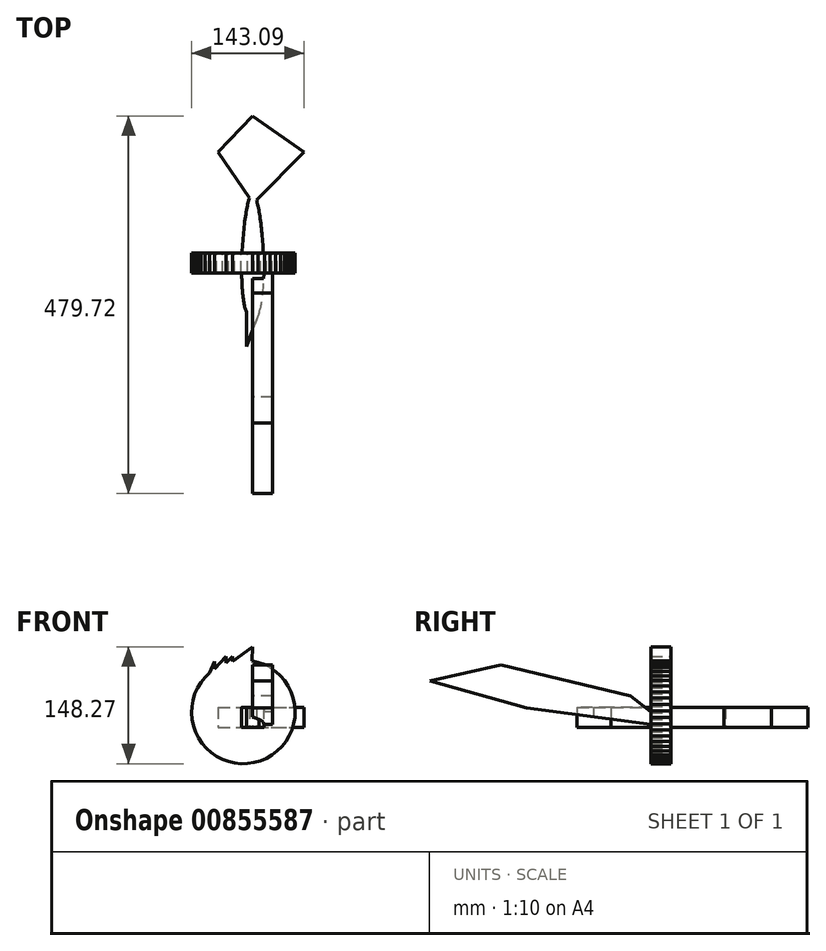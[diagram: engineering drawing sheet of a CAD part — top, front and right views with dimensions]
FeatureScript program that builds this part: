
annotation { "Feature Type Name" : "Feature", "Feature Type Description" : "" }
export const myFeature = defineFeature(function(context is Context, id is Id, definition is map)
    precondition{}
    {
        {
            var Q0;
            Q0=qCreatedBy(makeId("Top.planeOp"),FACE);
            var sketch = newSketch(context, id + "F0", { "sketchPlane" : qUnion([Q0])});
            skFitSpline(sketch, "E0", {"points": [v(0, 75.5) * mm, v(-7.53, -76.07) * mm, v(7.83, -76.02) * mm, v(0, 75.5) * mm]});
            skLineSegment(sketch, "E1", {"start": v(-7.53, -76.07) * mm, "end": v(-7.53, -118.78) * mm});
            skLineSegment(sketch, "E2", {"start": v(-7.53, -118.78) * mm, "end": v(7.83, -76.02) * mm});
            skLineSegment(sketch, "E3", {"start": v(-4.05, 69.83) * mm, "end": v(10.3, 128.02) * mm});
            skLineSegment(sketch, "E4", {"start": v(10.3, 128.02) * mm, "end": v(4.84, 67.53) * mm});
            skLineSegment(sketch, "E5", {"start": v(4.84, 67.53) * mm, "end": v(65.48, 128.02) * mm});
            skLineSegment(sketch, "E6", {"start": v(65.48, 128.02) * mm, "end": v(-44.03, 128.02) * mm});
            skLineSegment(sketch, "E7", {"start": v(-44.03, 128.02) * mm, "end": v(-4.05, 69.83) * mm});
            skLineSegment(sketch, "E8", {"start": v(-44.03, 128.02) * mm, "end": v(0, 174.22) * mm});
            skLineSegment(sketch, "E9", {"start": v(0, 174.22) * mm, "end": v(65.48, 128.02) * mm});
            skSolve(sketch);
        }
        {
            var Q0;
            Q0 = qSketchRegion(id + "F0", true);
            extrude(context, id + "F1", {"entities" : qUnion([Q0]), "depth" : 25.4 * mm, "offsetDistance" : 25.4 * mm});
        }
        {
            var Q0;
            Q0=qCreatedBy(makeId("Front.planeOp"),FACE);
            var sketch = newSketch(context, id + "F2", { "sketchPlane" : qUnion([Q0])});
            skCircle(sketch, "E10.cCircle", {"center": v(-11.87, 19.5) * mm, "radius": 65.76 * mm, "construction": true});
            skLineSegment(sketch, "E10.0", {"start": v(28.92, 71.09) * mm, "end": v(35.06, 65.57) * mm});
            skLineSegment(sketch, "E10.1", {"start": v(35.06, 65.57) * mm, "end": v(40.47, 59.32) * mm});
            skLineSegment(sketch, "E10.2", {"start": v(40.47, 59.32) * mm, "end": v(45.04, 52.45) * mm});
            skLineSegment(sketch, "E10.3", {"start": v(45.04, 52.45) * mm, "end": v(48.72, 45.05) * mm});
            skLineSegment(sketch, "E10.4", {"start": v(48.72, 45.05) * mm, "end": v(51.45, 37.26) * mm});
            skLineSegment(sketch, "E10.5", {"start": v(51.45, 37.26) * mm, "end": v(53.17, 29.18) * mm});
            skLineSegment(sketch, "E10.6", {"start": v(53.17, 29.18) * mm, "end": v(53.87, 20.95) * mm});
            skLineSegment(sketch, "E10.7", {"start": v(53.87, 20.95) * mm, "end": v(53.54, 12.7) * mm});
            skLineSegment(sketch, "E10.8", {"start": v(53.54, 12.7) * mm, "end": v(52.17, 4.56) * mm});
            skLineSegment(sketch, "E10.9", {"start": v(52.17, 4.56) * mm, "end": v(49.8, -3.35) * mm});
            skLineSegment(sketch, "E10.10", {"start": v(49.8, -3.35) * mm, "end": v(46.44, -10.9) * mm});
            skLineSegment(sketch, "E10.11", {"start": v(46.44, -10.9) * mm, "end": v(42.17, -17.96) * mm});
            skLineSegment(sketch, "E10.12", {"start": v(42.17, -17.96) * mm, "end": v(37.05, -24.44) * mm});
            skLineSegment(sketch, "E10.13", {"start": v(37.05, -24.44) * mm, "end": v(31.15, -30.23) * mm});
            skLineSegment(sketch, "E10.14", {"start": v(31.15, -30.23) * mm, "end": v(24.58, -35.23) * mm});
            skLineSegment(sketch, "E10.15", {"start": v(24.58, -35.23) * mm, "end": v(17.43, -39.36) * mm});
            skLineSegment(sketch, "E10.16", {"start": v(17.43, -39.36) * mm, "end": v(9.82, -42.57) * mm});
            skLineSegment(sketch, "E10.17", {"start": v(9.82, -42.57) * mm, "end": v(1.87, -44.8) * mm});
            skLineSegment(sketch, "E10.18", {"start": v(1.87, -44.8) * mm, "end": v(-6.3, -46.02) * mm});
            skLineSegment(sketch, "E10.19", {"start": v(-6.3, -46.02) * mm, "end": v(-14.55, -46.2) * mm});
            skLineSegment(sketch, "E10.20", {"start": v(-14.55, -46.2) * mm, "end": v(-22.76, -45.34) * mm});
            skLineSegment(sketch, "E10.21", {"start": v(-22.76, -45.34) * mm, "end": v(-30.8, -43.47) * mm});
            skLineSegment(sketch, "E10.22", {"start": v(-30.8, -43.47) * mm, "end": v(-38.55, -40.6) * mm});
            skLineSegment(sketch, "E10.23", {"start": v(-38.55, -40.6) * mm, "end": v(-45.87, -36.78) * mm});
            skLineSegment(sketch, "E10.24", {"start": v(-45.87, -36.78) * mm, "end": v(-52.66, -32.07) * mm});
            skLineSegment(sketch, "E10.25", {"start": v(-52.66, -32.07) * mm, "end": v(-58.8, -26.55) * mm});
            skLineSegment(sketch, "E10.26", {"start": v(-58.8, -26.55) * mm, "end": v(-64.2, -20.3) * mm});
            skLineSegment(sketch, "E10.27", {"start": v(-64.2, -20.3) * mm, "end": v(-68.78, -13.43) * mm});
            skLineSegment(sketch, "E10.28", {"start": v(-68.78, -13.43) * mm, "end": v(-72.46, -6.04) * mm});
            skLineSegment(sketch, "E10.29", {"start": v(-72.46, -6.04) * mm, "end": v(-75.18, 1.75) * mm});
            skLineSegment(sketch, "E10.30", {"start": v(-75.18, 1.75) * mm, "end": v(-76.91, 9.83) * mm});
            skLineSegment(sketch, "E10.31", {"start": v(-76.91, 9.83) * mm, "end": v(-77.61, 18.06) * mm});
            skLineSegment(sketch, "E10.32", {"start": v(-77.61, 18.06) * mm, "end": v(-77.27, 26.3) * mm});
            skLineSegment(sketch, "E10.33", {"start": v(-77.27, 26.3) * mm, "end": v(-75.9, 34.45) * mm});
            skLineSegment(sketch, "E10.34", {"start": v(-75.9, 34.45) * mm, "end": v(-73.53, 42.36) * mm});
            skLineSegment(sketch, "E10.35", {"start": v(-73.53, 42.36) * mm, "end": v(-70.18, 49.9) * mm});
            skLineSegment(sketch, "E10.36", {"start": v(-70.18, 49.9) * mm, "end": v(-65.9, 56.98) * mm});
            skLineSegment(sketch, "E10.37", {"start": v(-65.9, 56.98) * mm, "end": v(-60.78, 63.45) * mm});
            skLineSegment(sketch, "E10.38", {"start": v(-60.78, 63.45) * mm, "end": v(-54.89, 69.24) * mm});
            skLineSegment(sketch, "E10.39", {"start": v(-54.89, 69.24) * mm, "end": v(-48.32, 74.24) * mm});
            skLineSegment(sketch, "E10.40", {"start": v(-48.32, 74.24) * mm, "end": v(-41.17, 78.38) * mm});
            skLineSegment(sketch, "E10.41", {"start": v(-41.17, 78.38) * mm, "end": v(-33.56, 81.58) * mm});
            skLineSegment(sketch, "E10.42", {"start": v(-33.56, 81.58) * mm, "end": v(-25.6, 83.81) * mm});
            skLineSegment(sketch, "E10.43", {"start": v(-25.6, 83.81) * mm, "end": v(-17.44, 85.03) * mm});
            skLineSegment(sketch, "E10.44", {"start": v(-17.44, 85.03) * mm, "end": v(-9.19, 85.21) * mm});
            skLineSegment(sketch, "E10.45", {"start": v(-9.19, 85.21) * mm, "end": v(-0.97, 84.36) * mm});
            skLineSegment(sketch, "E10.46", {"start": v(-0.97, 84.36) * mm, "end": v(7.07, 82.48) * mm});
            skLineSegment(sketch, "E10.47", {"start": v(7.07, 82.48) * mm, "end": v(14.81, 79.6) * mm});
            skLineSegment(sketch, "E10.48", {"start": v(14.81, 79.6) * mm, "end": v(22.14, 75.8) * mm});
            skLineSegment(sketch, "E10.49", {"start": v(22.14, 75.8) * mm, "end": v(28.92, 71.09) * mm});
            skLineSegment(sketch, "E11", {"start": v(-54.89, 69.24) * mm, "end": v(-48.32, 83.6) * mm});
            skLineSegment(sketch, "E12", {"start": v(-48.32, 83.6) * mm, "end": v(-48.32, 74.24) * mm});
            skLineSegment(sketch, "E13", {"start": v(-48.32, 74.24) * mm, "end": v(-33.56, 90.15) * mm});
            skLineSegment(sketch, "E14", {"start": v(-33.56, 90.15) * mm, "end": v(-33.56, 81.58) * mm});
            skLineSegment(sketch, "E15", {"start": v(-33.56, 81.58) * mm, "end": v(-25.6, 90.15) * mm});
            skLineSegment(sketch, "E16", {"start": v(-25.6, 90.15) * mm, "end": v(-25.6, 83.81) * mm});
            skLineSegment(sketch, "E17", {"start": v(-25.6, 83.81) * mm, "end": v(0, 102.07) * mm});
            skLineSegment(sketch, "E18", {"start": v(0, 102.07) * mm, "end": v(-0.97, 84.36) * mm});
            skSolve(sketch);
        }
        {
            var Q0;
            Q0 = qSketchRegion(id + "F2", true);
            extrude(context, id + "F3", {"entities" : qUnion([Q0]), "operationType" : NewBodyOperationType.ADD, "depth" : 25.4 * mm, "offsetDistance" : 25.4 * mm});
        }
        {
            var Q0;
            Q0=qCreatedBy(makeId("Right.planeOp"),FACE);
            var sketch = newSketch(context, id + "F4", { "sketchPlane" : qUnion([Q0])});
            skLineSegment(sketch, "E19", {"start": v(-183.25, 24.49) * mm, "end": v(-305.5, 58.74) * mm});
            skLineSegment(sketch, "E20", {"start": v(-305.5, 58.74) * mm, "end": v(-215.7, 79.07) * mm});
            skLineSegment(sketch, "E21", {"start": v(-215.7, 79.07) * mm, "end": v(-183.25, 24.49) * mm});
            skLineSegment(sketch, "E22", {"start": v(-215.7, 79.07) * mm, "end": v(-50.86, 39.66) * mm});
            skLineSegment(sketch, "E23", {"start": v(-50.86, 39.66) * mm, "end": v(0, 0) * mm});
            skLineSegment(sketch, "E24", {"start": v(0, 0) * mm, "end": v(-183.25, 24.49) * mm});
            skSolve(sketch);
        }
        {
            var Q0;
            Q0 = qSketchRegion(id + "F4", true);
            extrude(context, id + "F5", {"entities" : qUnion([Q0]), "operationType" : NewBodyOperationType.ADD, "depth" : 25.4 * mm, "offsetDistance" : 25.4 * mm});
        }
    });
